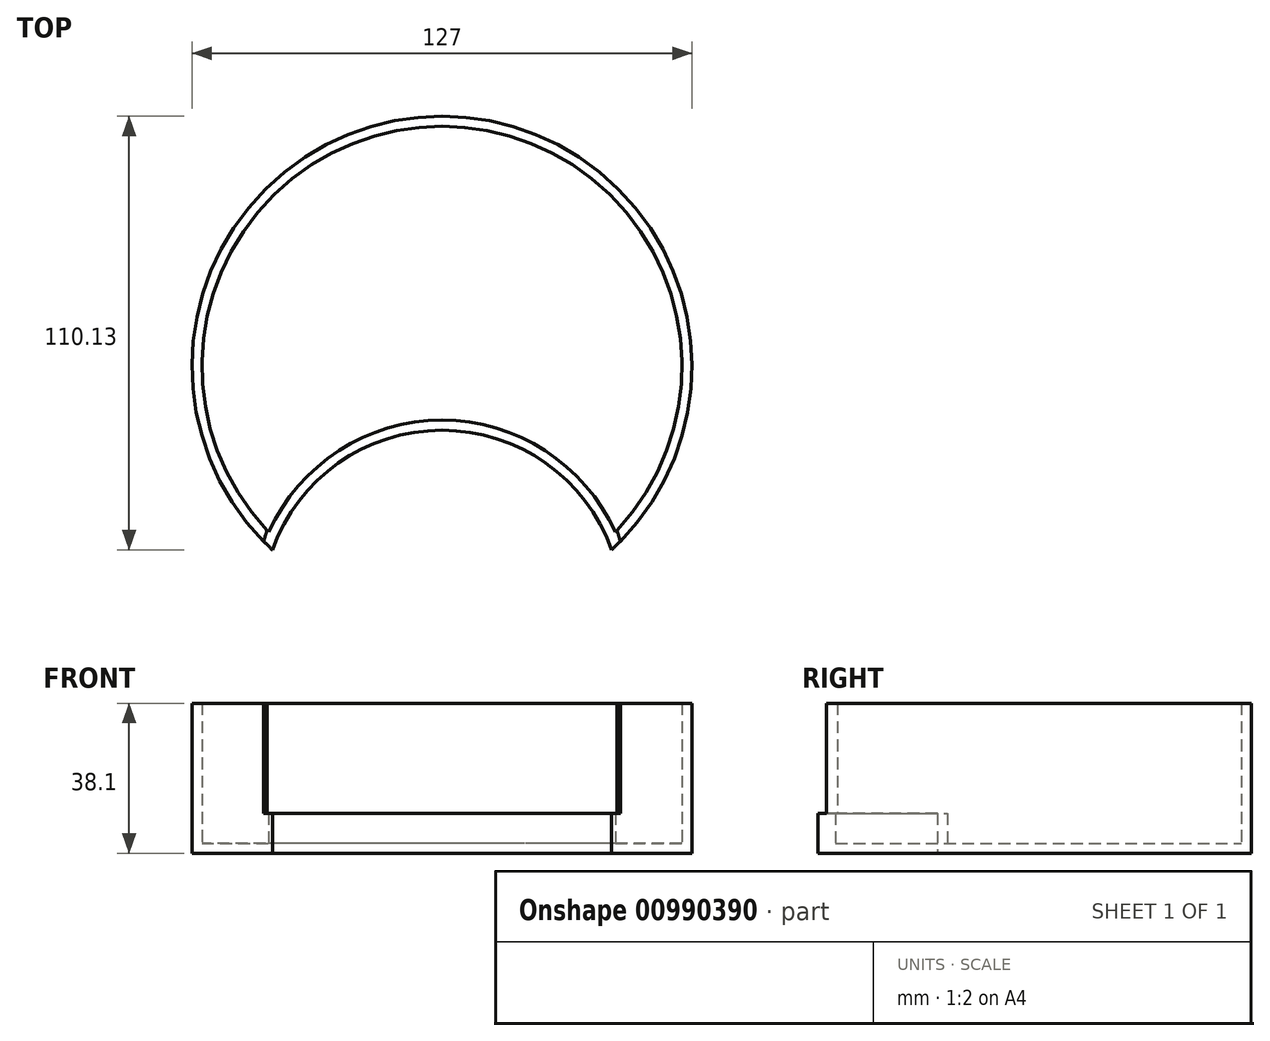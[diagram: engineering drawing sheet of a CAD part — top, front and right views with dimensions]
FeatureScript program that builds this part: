
annotation { "Feature Type Name" : "Feature", "Feature Type Description" : "" }
export const myFeature = defineFeature(function(context is Context, id is Id, definition is map)
    precondition{}
    {
        {
            var Q0;
            Q0=qCreatedBy(makeId("Top.planeOp"),FACE);
            var sketch = newSketch(context, id + "F0", { "sketchPlane" : qUnion([Q0])});
            skCircle(sketch, "E0", {"center": v(0, 0) * mm, "radius": 63.5 * mm});
            skSolve(sketch);
        }
        {
            var Q0;
            Q0=makeQuery(id+"F0.imprint","IMPRINT",FACE,{"disambiguationData":[TD([[makeQuery(id+"F0.imprint","IMPRINT",EDGE,{"derivedFrom":sQuery(id+"F0.wireOp",EDGE,"E0")}),1.0]])]});
            extrude(context, id + "F1", {"entities" : qUnion([Q0]), "depth" : 2.54 * mm, "offsetDistance" : 25.4 * mm});
        }
        {
            var Q0;
            Q0=qCreatedBy(makeId("Top.planeOp"),FACE);
            var sketch = newSketch(context, id + "F2", { "sketchPlane" : qUnion([Q0])});
            skCircle(sketch, "E1", {"center": v(0, -62.03) * mm, "radius": 45.77 * mm});
            skSolve(sketch);
        }
        {
            var Q0;
            Q0=makeQuery(id+"F2.imprint","IMPRINT",FACE,{"disambiguationData":[TD([[makeQuery(id+"F2.imprint","IMPRINT",EDGE,{"derivedFrom":sQuery(id+"F2.wireOp",EDGE,"E1")}),1.0]])]});
            var Q1;
            Q1=sQuery(id+"F2.wireOp",EDGE,"E1");
            extrude(context, id + "F3", {"entities" : qUnion([Q0]), "operationType" : NewBodyOperationType.REMOVE, "surfaceEntities" : qUnion([Q1]), "depth" : 25.4 * mm, "offsetDistance" : 25.4 * mm});
        }
        {
            var Q0;
            Q0=makeQuery(id+"F1.opExtrude","CAP_FACE",FACE,{"disambiguationData":[OSD([sQuery(id+"F0.wireOp",EDGE,"E0")])],"isStart":false});
            extrude(context, id + "F4", {"entities" : qUnion([Q0]), "operationType" : NewBodyOperationType.ADD, "oppositeDirection" : true, "depth" : 12.7 * mm, "offsetDistance" : 25.4 * mm});
        }
        {
            var Q0;
            Q0=makeQuery(id+"F1.opExtrude","CAP_FACE",FACE,{"disambiguationData":[OSD([sQuery(id+"F0.wireOp",EDGE,"E0")])],"isStart":false});
            extrude(context, id + "F5", {"entities" : qUnion([Q0]), "operationType" : NewBodyOperationType.ADD, "depth" : 25.4 * mm, "offsetDistance" : 25.4 * mm});
        }
        {
            var Q0;
            Q0=makeQuery(id+"F5.opExtrude","CAP_FACE",FACE,{"disambiguationData":[OSD([sQuery(id+"F0.wireOp",EDGE,"E0")])],"isStart":false});
            shell(context, id + "F6", {"entities" : qUnion([Q0]), "thickness" : 2.54 * mm});
        }
        {
            var Q0;
            Q0=qCreatedBy(makeId("Top.planeOp"),FACE);
            var sketch = newSketch(context, id + "F7", { "sketchPlane" : qUnion([Q0])});
            skCircle(sketch, "E2", {"center": v(0, -56.6) * mm, "radius": 46.87 * mm});
            skSolve(sketch);
        }
        {
            var Q0;
            Q0=makeQuery(id+"F7.imprint","IMPRINT",FACE,{"disambiguationData":[TD([[makeQuery(id+"F7.imprint","IMPRINT",EDGE,{"derivedFrom":sQuery(id+"F7.wireOp",EDGE,"E2")}),1.0]])]});
            var sketch = newSketch(context, id + "F8", { "sketchPlane" : qUnion([Q0])});
            skSolve(sketch);
        }
        {
            var Q0;
            Q0=makeQuery(id+"F8.imprint","IMPRINT",FACE,{"disambiguationData":[TD([[makeQuery(id+"F8.imprint","IMPRINT",EDGE,{"derivedFrom":makeQuery(id+"F7.imprint","IMPRINT",EDGE,{"derivedFrom":sQuery(id+"F7.wireOp",EDGE,"E2")})}),1.0]])]});
            extrude(context, id + "F9", {"entities" : qUnion([Q0]), "operationType" : NewBodyOperationType.REMOVE, "depth" : 177.8 * mm, "offsetDistance" : 25.4 * mm});
        }
    });
